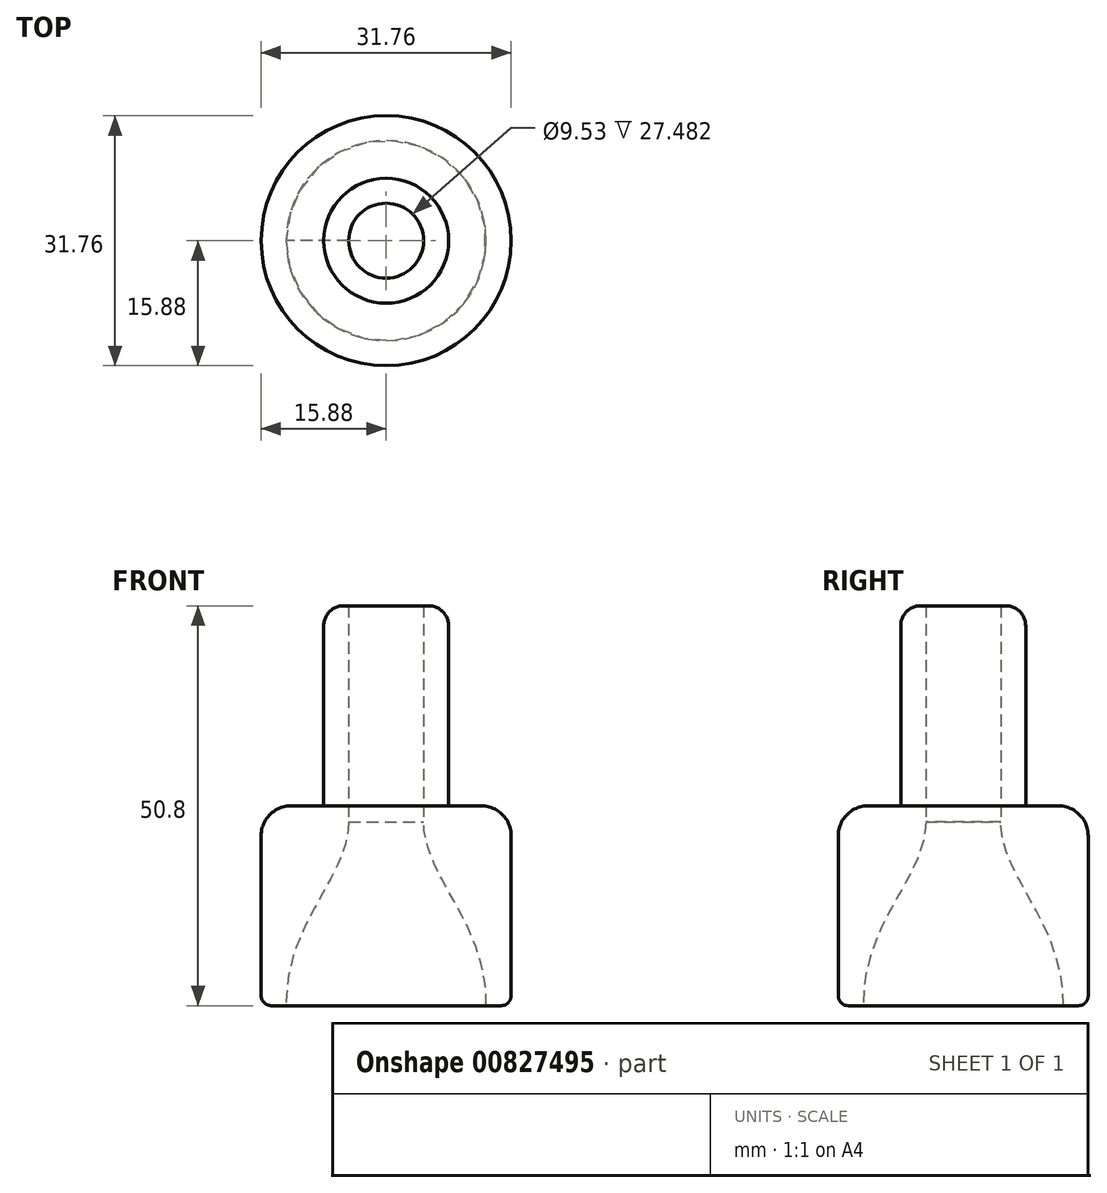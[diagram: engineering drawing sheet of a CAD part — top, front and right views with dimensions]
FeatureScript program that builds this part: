
annotation { "Feature Type Name" : "Feature", "Feature Type Description" : "" }
export const myFeature = defineFeature(function(context is Context, id is Id, definition is map)
    precondition{}
    {
        {
            var Q0;
            Q0=qCreatedBy(makeId("Front.planeOp"),FACE);
            var sketch = newSketch(context, id + "F0", { "sketchPlane" : qUnion([Q0])});
            skLineSegment(sketch, "E0", {"start": v(-15.88, 2.54) * mm, "end": v(-15.88, 22.86) * mm});
            skLineSegment(sketch, "E1", {"start": v(-7.94, 49.53) * mm, "end": v(-7.94, 26.67) * mm});
            skLineSegment(sketch, "E2", {"start": v(-12.07, 26.67) * mm, "end": v(-7.94, 26.67) * mm});
            skLineSegment(sketch, "E3", {"start": v(-5.4, 52.07) * mm, "end": v(-4.76, 52.07) * mm});
            skLineSegment(sketch, "E4", {"start": v(-4.76, 52.07) * mm, "end": v(-4.76, 24.59) * mm});
            skLineSegment(sketch, "E5", {"start": v(-14.6, 1.27) * mm, "end": v(-12.7, 1.27) * mm});
            skFitSpline(sketch, "E6", {"points": [v(-4.76, 24.59) * mm, v(-12.7, 1.27) * mm], "startDerivative": vector(-0.45, -21.9) * mm, "endDerivative": vector(0.3, -31.88) * mm});
            skPoint(sketch, "E7.visualSharp", {"position": v(-15.88, 26.67) * mm});
            skArc(sketch, "E7.filletArc", {"start": v(-12.07, 26.67) * mm, "mid": v(-14.76, 25.55) * mm, "end": v(-15.88, 22.86) * mm});
            skLineSegment(sketch, "E8", {"start": v(0, 0) * mm, "end": v(0, 51.07) * mm, "construction": true});
            skPoint(sketch, "E9.visualSharp", {"position": v(-7.94, 52.07) * mm});
            skArc(sketch, "E9.filletArc", {"start": v(-5.4, 52.07) * mm, "mid": v(-7.2, 51.33) * mm, "end": v(-7.94, 49.53) * mm});
            skPoint(sketch, "E10.visualSharp", {"position": v(-15.88, 1.27) * mm});
            skArc(sketch, "E10.filletArc", {"start": v(-15.88, 2.54) * mm, "mid": v(-15.5, 1.64) * mm, "end": v(-14.6, 1.27) * mm});
            skSolve(sketch);
        }
        {
            var Q0;
            Q0=makeQuery(id+"F0.imprint","IMPRINT",FACE,{"disambiguationData":[TD([[makeQuery(id+"F0.imprint","IMPRINT",EDGE,{"derivedFrom":sQuery(id+"F0.wireOp",EDGE,"E0")}),-1.0]])]});
            var Q1;
            Q1=sQuery(id+"F0.wireOp",EDGE,"E8");
            revolve(context, id + "F1", {"surfaceOperationType" : NewSurfaceOperationType.NEW, "entities" : qUnion([Q0]), "axis" : qUnion([Q1]), "revolveType" : RevolveType.FULL});
        }
    });
